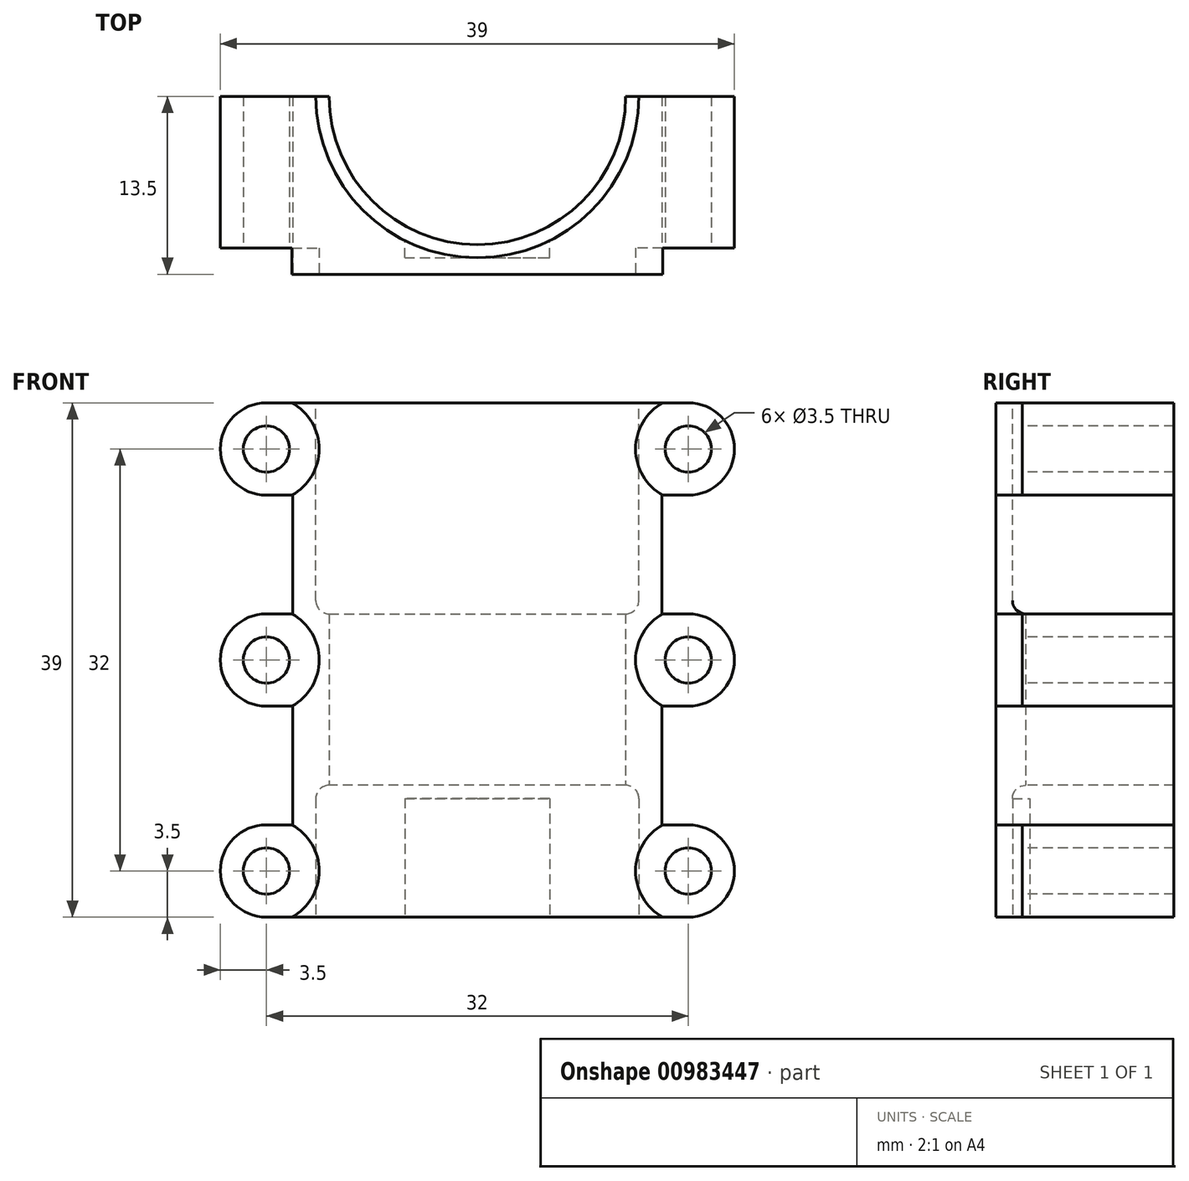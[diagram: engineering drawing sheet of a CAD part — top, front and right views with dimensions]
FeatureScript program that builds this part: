
annotation { "Feature Type Name" : "Feature", "Feature Type Description" : "" }
export const myFeature = defineFeature(function(context is Context, id is Id, definition is map)
    precondition{}
    {
        {
            var Q0;
            Q0=qCreatedBy(makeId("Top.planeOp"),FACE);
            var sketch = newSketch(context, id + "F0", { "sketchPlane" : qUnion([Q0])});
            skCircle(sketch, "E0", {"center": v(0, 0) * mm, "radius": 11.25 * mm});
            skSolve(sketch);
        }
        {
            var Q0;
            Q0=qSketchRegion(id+"F0",true);
            extrude(context, id + "F1", {"entities" : qUnion([Q0]), "depth" : 39 * mm, "offsetDistance" : 25 * mm});
        }
        {
            var Q0;
            Q0=makeQuery(id+"F1.opExtrude","CAP_FACE",FACE,{"disambiguationData":[OSD([sQuery(id+"F0.wireOp",EDGE,"E0")])],"isStart":false});
            var sketch = newSketch(context, id + "F2", { "sketchPlane" : qUnion([Q0])});
            skCircle(sketch, "E1", {"center": v(0, 0) * mm, "radius": 12.25 * mm});
            skSolve(sketch);
        }
        {
            var Q0;
            Q0=makeQuery(id+"F2.imprint","IMPRINT",FACE,{"disambiguationData":[TD([[makeQuery(id+"F2.imprint","IMPRINT",EDGE,{"derivedFrom":sQuery(id+"F2.wireOp",EDGE,"E1")}),1.0]])]});
            extrude(context, id + "F3", {"entities" : qUnion([Q0]), "operationType" : NewBodyOperationType.ADD, "oppositeDirection" : true, "depth" : 16 * mm, "offsetDistance" : 25 * mm});
        }
        {
            var Q0;
            Q0=makeQuery(id+"F1.opExtrude","CAP_FACE",FACE,{"disambiguationData":[OSD([sQuery(id+"F0.wireOp",EDGE,"E0")])],"isStart":true});
            var sketch = newSketch(context, id + "F4", { "sketchPlane" : qUnion([Q0])});
            skCircle(sketch, "E2", {"center": v(0, 0) * mm, "radius": 12.25 * mm});
            skSolve(sketch);
        }
        {
            var Q0;
            Q0=makeQuery(id+"F3.opExtrude","CAP_EDGE",EDGE,{"disambiguationData":[OSD([sQuery(id+"F2.wireOp",EDGE,"E1")])],"isStart":false});
            fillet(context, id + "F5", {"entities" : qUnion([Q0]), "radius" : 1 * mm, "tangentPropagation" : true, "allowEdgeOverflow" : false});
        }
        {
            var Q0;
            Q0=makeQuery(id+"F4.imprint","IMPRINT",FACE,{"disambiguationData":[TD([[makeQuery(id+"F4.imprint","IMPRINT",EDGE,{"derivedFrom":sQuery(id+"F4.wireOp",EDGE,"E2")}),1.0]])]});
            extrude(context, id + "F6", {"entities" : qUnion([Q0]), "operationType" : NewBodyOperationType.ADD, "oppositeDirection" : true, "depth" : 10 * mm, "offsetDistance" : 25 * mm});
        }
        {
            var Q0;
            Q0=makeQuery(id+"F6.opExtrude","CAP_EDGE",EDGE,{"disambiguationData":[OSD([sQuery(id+"F4.wireOp",EDGE,"E2")])],"isStart":false});
            fillet(context, id + "F7", {"entities" : qUnion([Q0]), "radius" : 1 * mm, "tangentPropagation" : true, "allowEdgeOverflow" : false});
        }
        {
            var Q0;
            {var subQ0=sQuery(id+"F0.wireOp",EDGE,"E0");Q0=makeQuery(id+"F6.boolean.opBoolean","MERGE",FACE,{"derivedFrom":[makeQuery(id+"F1.opExtrude","CAP_FACE",FACE,{"disambiguationData":[OSD([subQ0])],"isStart":true}),makeQuery(id+"F6.opExtrude","CAP_FACE",FACE,{"disambiguationData":[OSD([subQ0,sQuery(id+"F4.wireOp",EDGE,"E2")])],"isStart":true})]});}
            var sketch = newSketch(context, id + "F8", { "sketchPlane" : qUnion([Q0])});
            skLineSegment(sketch, "E3.bottom", {"start": v(-5.5, 12.25) * mm, "end": v(5.5, 12.25) * mm});
            skLineSegment(sketch, "E3.top", {"start": v(-5.5, 10.25) * mm, "end": v(5.5, 10.25) * mm});
            skLineSegment(sketch, "E3.left", {"start": v(-5.5, 12.25) * mm, "end": v(-5.5, 10.25) * mm});
            skLineSegment(sketch, "E3.right", {"start": v(5.5, 12.25) * mm, "end": v(5.5, 10.25) * mm});
            skPoint(sketch, "E3.middle", {"position": v(0, 11.25) * mm});
            skSolve(sketch);
        }
        {
            var Q0;
            {var subQ0=sQuery(id+"F8.wireOp",EDGE,"E3.left");var subQ1=sQuery(id+"F8.wireOp",EDGE,"E3.bottom");var subQ2=makeQuery(id+"F8.imprint","INTERSECT",VERTEX,{"derivedFrom":[subQ1,subQ0]});Q0=makeQuery(id+"F8.imprint","IMPRINT",FACE,{"disambiguationData":[TD([[makeQuery(id+"F8.imprint","IMPRINT",EDGE,{"disambiguationData":[TD([[subQ2,-1.0]])],"derivedFrom":subQ1}),-1.0]])]});}
            var Q1;
            {var subQ0=sQuery(id+"F8.wireOp",EDGE,"E3.right");var subQ1=sQuery(id+"F8.wireOp",EDGE,"E3.bottom");var subQ2=makeQuery(id+"F8.imprint","INTERSECT",VERTEX,{"derivedFrom":[subQ1,subQ0]});Q1=makeQuery(id+"F8.imprint","IMPRINT",FACE,{"disambiguationData":[TD([[makeQuery(id+"F8.imprint","IMPRINT",EDGE,{"disambiguationData":[TD([[subQ2,1.0]])],"derivedFrom":subQ1}),-1.0]])]});}
            extrude(context, id + "F9", {"entities" : qUnion([Q0, Q1]), "operationType" : NewBodyOperationType.ADD, "oppositeDirection" : true, "depth" : 9 * mm, "offsetDistance" : 25 * mm});
        }
        {
            var Q0;
            {var subQ0=sQuery(id+"F8.wireOp",EDGE,"E3.bottom");var subQ1=sQuery(id+"F4.wireOp",EDGE,"E2");var subQ2=sQuery(id+"F0.wireOp",EDGE,"E0");Q0=makeQuery(id+"F9.boolean.opBoolean","MERGE",FACE,{"derivedFrom":[makeQuery(id+"F6.boolean.opBoolean","MERGE",FACE,{"derivedFrom":[makeQuery(id+"F1.opExtrude","CAP_FACE",FACE,{"disambiguationData":[OSD([subQ2])],"isStart":true}),makeQuery(id+"F6.opExtrude","CAP_FACE",FACE,{"disambiguationData":[OSD([subQ2,subQ1])],"isStart":true})]}),makeQuery(id+"F9.opExtrude","CAP_FACE",FACE,{"disambiguationData":[OSD([subQ1,subQ0,sQuery(id+"F8.wireOp",EDGE,"E3.left")])],"isStart":true}),makeQuery(id+"F9.opExtrude","CAP_FACE",FACE,{"disambiguationData":[OSD([subQ1,subQ0,sQuery(id+"F8.wireOp",EDGE,"E3.right")])],"isStart":true})]});}
            var sketch = newSketch(context, id + "F10", { "sketchPlane" : qUnion([Q0])});
            skLineSegment(sketch, "E4.bottom", {"start": v(-7.5, -8.25) * mm, "end": v(7.5, -8.25) * mm});
            skLineSegment(sketch, "E4.top", {"start": v(-7.5, -12.25) * mm, "end": v(7.5, -12.25) * mm});
            skLineSegment(sketch, "E4.left", {"start": v(-7.5, -8.25) * mm, "end": v(-7.5, -12.25) * mm});
            skLineSegment(sketch, "E4.right", {"start": v(7.5, -8.25) * mm, "end": v(7.5, -12.25) * mm});
            skPoint(sketch, "E4.middle", {"position": v(0, -10.25) * mm});
            skSolve(sketch);
        }
        {
            var Q0;
            {var subQ0=sQuery(id+"F10.wireOp",EDGE,"E4.right");var subQ1=sQuery(id+"F10.wireOp",EDGE,"E4.top");var subQ2=makeQuery(id+"F10.imprint","INTERSECT",VERTEX,{"derivedFrom":[subQ1,subQ0]});Q0=makeQuery(id+"F10.imprint","IMPRINT",FACE,{"disambiguationData":[TD([[makeQuery(id+"F10.imprint","IMPRINT",EDGE,{"disambiguationData":[TD([[subQ2,1.0]])],"derivedFrom":subQ1}),1.0]])]});}
            var Q1;
            {var subQ0=sQuery(id+"F10.wireOp",EDGE,"E4.left");var subQ1=sQuery(id+"F10.wireOp",EDGE,"E4.top");var subQ2=makeQuery(id+"F10.imprint","INTERSECT",VERTEX,{"derivedFrom":[subQ1,subQ0]});Q1=makeQuery(id+"F10.imprint","IMPRINT",FACE,{"disambiguationData":[TD([[makeQuery(id+"F10.imprint","IMPRINT",EDGE,{"disambiguationData":[TD([[subQ2,-1.0]])],"derivedFrom":subQ1}),1.0]])]});}
            var Q2;
            {var subQ4=sQuery(id+"F10.wireOp",EDGE,"E4.bottom");Q2=makeQuery(id+"F10.imprint","IMPRINT",FACE,{"disambiguationData":[TD([[makeQuery(id+"F10.imprint","IMPRINT",EDGE,{"derivedFrom":subQ4}),-1.0]])]});}
            extrude(context, id + "F11", {"entities" : qUnion([Q0, Q1, Q2]), "operationType" : NewBodyOperationType.ADD, "oppositeDirection" : true, "depth" : 39 * mm, "offsetDistance" : 25 * mm});
        }
        {
            var Q0;
            Q0=makeQuery(id+"F11.opExtrude","SWEPT_FACE",FACE,{"disambiguationData":[OSD([sQuery(id+"F10.wireOp",EDGE,"E4.top")])]});
            var sketch = newSketch(context, id + "F12", { "sketchPlane" : qUnion([Q0])});
            skLineSegment(sketch, "E5.bottom", {"start": v(-11, 12) * mm, "end": v(-7.5, 12) * mm});
            skLineSegment(sketch, "E5.top", {"start": v(-11, 6.5) * mm, "end": v(-7.5, 6.5) * mm});
            skLineSegment(sketch, "E5.left", {"start": v(-11, 12) * mm, "end": v(-11, 6.5) * mm});
            skLineSegment(sketch, "E5.right", {"start": v(-7.5, 12) * mm, "end": v(-7.5, 6.5) * mm});
            skSolve(sketch);
        }
        {
            var Q0;
            Q0=makeQuery(id+"F12.imprint","IMPRINT",FACE,{"disambiguationData":[TD([[makeQuery(id+"F12.imprint","IMPRINT",EDGE,{"derivedFrom":sQuery(id+"F12.wireOp",EDGE,"E5.bottom")}),-1.0]])]});
            extrude(context, id + "F13", {"entities" : qUnion([Q0]), "operationType" : NewBodyOperationType.ADD, "depth" : 2 * mm, "offsetDistance" : 25 * mm, "hasSecondDirection" : true, "secondDirectionOppositeDirection" : true, "secondDirectionDepth" : 12 * mm});
        }
        {
            var Q0;
            Q0=makeQuery(id+"F11.opExtrude","SWEPT_FACE",FACE,{"disambiguationData":[OSD([sQuery(id+"F10.wireOp",EDGE,"E4.top")])]});
            var sketch = newSketch(context, id + "F14", { "sketchPlane" : qUnion([Q0])});
            skCircle(sketch, "E6", {"center": v(-0.06, 19) * mm, "radius": 6.5 * mm});
            skSolve(sketch);
        }
        {
            var Q0;
            Q0=makeQuery(id+"F14.imprint","IMPRINT",FACE,{"disambiguationData":[TD([[makeQuery(id+"F14.imprint","IMPRINT",EDGE,{"derivedFrom":sQuery(id+"F14.wireOp",EDGE,"E6")}),1.0]])]});
            extrude(context, id + "F15", {"entities" : qUnion([Q0]), "operationType" : NewBodyOperationType.ADD, "depth" : 2 * mm, "offsetDistance" : 25 * mm});
        }
        {
            var Q0;
            Q0=makeQuery(id+"F11.opExtrude","SWEPT_FACE",FACE,{"disambiguationData":[OSD([sQuery(id+"F10.wireOp",EDGE,"E4.top")])]});
            var sketch = newSketch(context, id + "F16", { "sketchPlane" : qUnion([Q0])});
            skLineSegment(sketch, "E7.bottom", {"start": v(-8, 27.5) * mm, "end": v(-4.5, 27.5) * mm});
            skLineSegment(sketch, "E7.top", {"start": v(-8, 31.5) * mm, "end": v(-4.5, 31.5) * mm});
            skLineSegment(sketch, "E7.left", {"start": v(-8, 27.5) * mm, "end": v(-8, 31.5) * mm});
            skLineSegment(sketch, "E7.right", {"start": v(-4.5, 27.5) * mm, "end": v(-4.5, 31.5) * mm});
            skSolve(sketch);
        }
        {
            var Q0;
            Q0=makeQuery(id+"F16.imprint","IMPRINT",FACE,{"disambiguationData":[TD([[makeQuery(id+"F16.imprint","IMPRINT",EDGE,{"derivedFrom":sQuery(id+"F16.wireOp",EDGE,"E7.bottom")}),1.0]])]});
            var Q1;
            {var subQ2=sQuery(id+"F16.wireOp",EDGE,"E7.right");Q1=makeQuery(id+"F16.imprint","IMPRINT",FACE,{"disambiguationData":[TD([[makeQuery(id+"F16.imprint","IMPRINT",EDGE,{"derivedFrom":subQ2}),1.0]])]});}
            extrude(context, id + "F17", {"entities" : qUnion([Q0, Q1]), "operationType" : NewBodyOperationType.ADD, "depth" : 6 * mm, "offsetDistance" : 25 * mm, "hasSecondDirection" : true, "secondDirectionOppositeDirection" : true, "secondDirectionDepth" : 16.7 * mm});
        }
        {
            var Q0;
            Q0=qCreatedBy(makeId("Front.planeOp"),FACE);
            var sketch = newSketch(context, id + "F18", { "sketchPlane" : qUnion([Q0])});
            skLineSegment(sketch, "E8.bottom", {"start": v(14, 0) * mm, "end": v(-14, 0) * mm});
            skLineSegment(sketch, "E8.top", {"start": v(14, 39) * mm, "end": v(-14, 39) * mm});
            skLineSegment(sketch, "E8.left", {"start": v(14, 0) * mm, "end": v(14, 39) * mm});
            skLineSegment(sketch, "E8.right", {"start": v(-14, 0) * mm, "end": v(-14, 39) * mm});
            skPoint(sketch, "E8.middle", {"position": v(0, 19.5) * mm});
            skSolve(sketch);
        }
        {
            var Q0;
            Q0=makeQuery(id+"F18.imprint","IMPRINT",FACE,{"disambiguationData":[TD([[makeQuery(id+"F18.imprint","IMPRINT",EDGE,{"derivedFrom":sQuery(id+"F18.wireOp",EDGE,"E8.bottom")}),-1.0]])]});
            extrude(context, id + "F19", {"entities" : qUnion([Q0]), "depth" : 13.5 * mm, "offsetDistance" : 25 * mm, "hasSecondDirection" : true, "secondDirectionOppositeDirection" : true, "secondDirectionDepth" : 12.2 * mm});
        }
        {
            var Q0;
            Q0=makeQuery(id+"F1.opExtrude","SWEPT_BODY",BODY,{"disambiguationData":[OSD([sQuery(id+"F0.wireOp",EDGE,"E0")])]});
            var Q1;
            Q1=makeQuery(id+"F19.opExtrude","SWEPT_BODY",BODY,{"disambiguationData":[OSD([sQuery(id+"F18.wireOp",EDGE,"E8.bottom"),sQuery(id+"F18.wireOp",EDGE,"E8.top"),sQuery(id+"F18.wireOp",EDGE,"E8.left"),sQuery(id+"F18.wireOp",EDGE,"E8.right")])]});
            booleanBodies(context, id + "F20", {"operationType" : BooleanOperationType.SUBTRACTION, "tools" : qUnion([Q0]), "targets" : qUnion([Q1])});
        }
        {
            var Q0;
            Q0=makeQuery(id+"F19.opExtrude","CAP_FACE",FACE,{"disambiguationData":[OSD([sQuery(id+"F18.wireOp",EDGE,"E8.bottom"),sQuery(id+"F18.wireOp",EDGE,"E8.top"),sQuery(id+"F18.wireOp",EDGE,"E8.left"),sQuery(id+"F18.wireOp",EDGE,"E8.right")])],"isStart":false});
            var sketch = newSketch(context, id + "F21", { "sketchPlane" : qUnion([Q0])});
            skLineSegment(sketch, "E9.bottom", {"start": v(16, 7) * mm, "end": v(-16, 7) * mm});
            skLineSegment(sketch, "E9.top", {"start": v(16, 0) * mm, "end": v(-16, 0) * mm});
            skLineSegment(sketch, "E9.left", {"start": v(19.5, 3.5) * mm, "end": v(19.5, 3.5) * mm});
            skLineSegment(sketch, "E9.right", {"start": v(-19.5, 3.5) * mm, "end": v(-19.5, 3.5) * mm});
            skPoint(sketch, "E9.middle", {"position": v(0, 3.5) * mm});
            skLineSegment(sketch, "E10.bottom", {"start": v(16, 39) * mm, "end": v(-16, 39) * mm});
            skLineSegment(sketch, "E10.top", {"start": v(16, 32) * mm, "end": v(-16, 32) * mm});
            skLineSegment(sketch, "E10.left", {"start": v(19.5, 35.5) * mm, "end": v(19.5, 35.5) * mm});
            skLineSegment(sketch, "E10.right", {"start": v(-19.5, 35.5) * mm, "end": v(-19.5, 35.5) * mm});
            skPoint(sketch, "E10.middle", {"position": v(0, 35.5) * mm});
            skPoint(sketch, "E11.visualSharp", {"position": v(-19.5, 0) * mm});
            skArc(sketch, "E11.filletArc", {"start": v(-19.5, 3.5) * mm, "mid": v(-18.47, 1.03) * mm, "end": v(-16, 0) * mm});
            skPoint(sketch, "E12.visualSharp", {"position": v(-19.5, 7) * mm});
            skArc(sketch, "E12.filletArc", {"start": v(-16, 7) * mm, "mid": v(-18.47, 5.97) * mm, "end": v(-19.5, 3.5) * mm});
            skPoint(sketch, "E13.visualSharp", {"position": v(-19.5, 32) * mm});
            skArc(sketch, "E13.filletArc", {"start": v(-19.5, 35.5) * mm, "mid": v(-18.47, 33.03) * mm, "end": v(-16, 32) * mm});
            skPoint(sketch, "E14.visualSharp", {"position": v(19.5, 39) * mm});
            skArc(sketch, "E14.filletArc", {"start": v(19.5, 35.5) * mm, "mid": v(18.47, 37.97) * mm, "end": v(16, 39) * mm});
            skPoint(sketch, "E15.visualSharp", {"position": v(19.5, 32) * mm});
            skArc(sketch, "E15.filletArc", {"start": v(16, 32) * mm, "mid": v(18.47, 33.03) * mm, "end": v(19.5, 35.5) * mm});
            skPoint(sketch, "E16.visualSharp", {"position": v(19.5, 0) * mm});
            skArc(sketch, "E16.filletArc", {"start": v(16, 0) * mm, "mid": v(18.47, 1.03) * mm, "end": v(19.5, 3.5) * mm});
            skPoint(sketch, "E17.visualSharp", {"position": v(-19.5, 39) * mm});
            skArc(sketch, "E17.filletArc", {"start": v(-16, 39) * mm, "mid": v(-18.47, 37.97) * mm, "end": v(-19.5, 35.5) * mm});
            skPoint(sketch, "E18.visualSharp", {"position": v(19.5, 7) * mm});
            skArc(sketch, "E18.filletArc", {"start": v(19.5, 3.5) * mm, "mid": v(18.47, 5.97) * mm, "end": v(16, 7) * mm});
            skCircle(sketch, "E19", {"center": v(-16, 35.5) * mm, "radius": 1.75 * mm});
            skCircle(sketch, "E20", {"center": v(16, 35.5) * mm, "radius": 1.75 * mm});
            skCircle(sketch, "E21", {"center": v(16, 3.5) * mm, "radius": 1.75 * mm});
            skCircle(sketch, "E22", {"center": v(-16, 3.5) * mm, "radius": 1.75 * mm});
            skLineSegment(sketch, "E23.bottom", {"start": v(16, 16) * mm, "end": v(-16, 16) * mm});
            skLineSegment(sketch, "E23.top", {"start": v(16, 23) * mm, "end": v(-16, 23) * mm});
            skLineSegment(sketch, "E23.left", {"start": v(19.5, 19.5) * mm, "end": v(19.5, 19.5) * mm});
            skLineSegment(sketch, "E23.right", {"start": v(-19.5, 19.5) * mm, "end": v(-19.5, 19.5) * mm});
            skPoint(sketch, "E23.middle", {"position": v(0, 19.5) * mm});
            skPoint(sketch, "E24.visualSharp", {"position": v(-19.5, 23) * mm});
            skArc(sketch, "E24.filletArc", {"start": v(-16, 23) * mm, "mid": v(-18.47, 21.97) * mm, "end": v(-19.5, 19.5) * mm});
            skPoint(sketch, "E25.visualSharp", {"position": v(-19.5, 16) * mm});
            skArc(sketch, "E25.filletArc", {"start": v(-19.5, 19.5) * mm, "mid": v(-18.47, 17.03) * mm, "end": v(-16, 16) * mm});
            skPoint(sketch, "E26.visualSharp", {"position": v(19.5, 16) * mm});
            skArc(sketch, "E26.filletArc", {"start": v(16, 16) * mm, "mid": v(18.47, 17.03) * mm, "end": v(19.5, 19.5) * mm});
            skPoint(sketch, "E27.visualSharp", {"position": v(19.5, 23) * mm});
            skArc(sketch, "E27.filletArc", {"start": v(19.5, 19.5) * mm, "mid": v(18.47, 21.97) * mm, "end": v(16, 23) * mm});
            skCircle(sketch, "E28", {"center": v(-16, 19.5) * mm, "radius": 1.75 * mm});
            skCircle(sketch, "E29", {"center": v(16, 19.5) * mm, "radius": 1.75 * mm});
            skSolve(sketch);
        }
        {
            var Q0;
            {var subQ0=sQuery(id+"F21.wireOp",EDGE,"E11.filletArc");Q0=makeQuery(id+"F21.imprint","IMPRINT",FACE,{"disambiguationData":[TD([[makeQuery(id+"F21.imprint","IMPRINT",EDGE,{"derivedFrom":subQ0}),1.0]])]});}
            var Q1;
            {var subQ5=sQuery(id+"F21.wireOp",EDGE,"E13.filletArc");Q1=makeQuery(id+"F21.imprint","IMPRINT",FACE,{"disambiguationData":[TD([[makeQuery(id+"F21.imprint","IMPRINT",EDGE,{"derivedFrom":subQ5}),1.0]])]});}
            var Q2;
            {var subQ5=sQuery(id+"F21.wireOp",EDGE,"E14.filletArc");Q2=makeQuery(id+"F21.imprint","IMPRINT",FACE,{"disambiguationData":[TD([[makeQuery(id+"F21.imprint","IMPRINT",EDGE,{"derivedFrom":subQ5}),1.0]])]});}
            var Q3;
            {var subQ4=sQuery(id+"F21.wireOp",EDGE,"E16.filletArc");Q3=makeQuery(id+"F21.imprint","IMPRINT",FACE,{"disambiguationData":[TD([[makeQuery(id+"F21.imprint","IMPRINT",EDGE,{"derivedFrom":subQ4}),1.0]])]});}
            var Q4;
            {var subQ4=sQuery(id+"F21.wireOp",EDGE,"E24.filletArc");var subQ6=sQuery(id+"F21.wireOp",EDGE,"E25.filletArc");var subQ7=makeQuery(id+"F21.imprint","INTERSECT",VERTEX,{"derivedFrom":[subQ4,subQ6]});Q4=makeQuery(id+"F21.imprint","IMPRINT",FACE,{"disambiguationData":[TD([[makeQuery(id+"F21.imprint","IMPRINT",EDGE,{"disambiguationData":[TD([[subQ7,1.0]])],"derivedFrom":subQ4}),1.0]])]});}
            var Q5;
            {var subQ0=sQuery(id+"F21.wireOp",EDGE,"E26.filletArc");var subQ6=sQuery(id+"F21.wireOp",EDGE,"E27.filletArc");var subQ7=makeQuery(id+"F21.imprint","INTERSECT",VERTEX,{"derivedFrom":[subQ0,subQ6]});Q5=makeQuery(id+"F21.imprint","IMPRINT",FACE,{"disambiguationData":[TD([[makeQuery(id+"F21.imprint","IMPRINT",EDGE,{"disambiguationData":[TD([[subQ7,1.0]])],"derivedFrom":subQ0}),1.0]])]});}
            extrude(context, id + "F22", {"entities" : qUnion([Q0, Q1, Q2, Q3, Q4, Q5]), "operationType" : NewBodyOperationType.ADD, "oppositeDirection" : true, "depth" : 25.7 * mm, "offsetDistance" : 25 * mm});
        }
        {
            var Q0;
            {var subQ0=sQuery(id+"F21.wireOp",EDGE,"E22");var subQ1=makeQuery(id+"F19.opExtrude","CAP_EDGE",EDGE,{"disambiguationData":[OSD([sQuery(id+"F18.wireOp",EDGE,"E8.right")])],"isStart":false});var subQ2=makeQuery(id+"F21.imprint","INTERSECT",VERTEX,{"disambiguationData":[OD(0.0)],"derivedFrom":[subQ1,subQ0]});Q0=makeQuery(id+"F21.imprint","IMPRINT",FACE,{"disambiguationData":[TD([[makeQuery(id+"F21.imprint","IMPRINT",EDGE,{"disambiguationData":[TD([[subQ2,-1.0]])],"derivedFrom":subQ0}),1.0]])]});}
            var Q1;
            {var subQ0=sQuery(id+"F21.wireOp",EDGE,"E21");var subQ1=makeQuery(id+"F19.opExtrude","CAP_EDGE",EDGE,{"disambiguationData":[OSD([sQuery(id+"F18.wireOp",EDGE,"E8.left")])],"isStart":false});var subQ2=makeQuery(id+"F21.imprint","INTERSECT",VERTEX,{"disambiguationData":[OD(0.0)],"derivedFrom":[subQ1,subQ0]});Q1=makeQuery(id+"F21.imprint","IMPRINT",FACE,{"disambiguationData":[TD([[makeQuery(id+"F21.imprint","IMPRINT",EDGE,{"disambiguationData":[TD([[subQ2,1.0]])],"derivedFrom":subQ0}),1.0]])]});}
            var Q2;
            {var subQ0=sQuery(id+"F21.wireOp",EDGE,"E20");var subQ1=makeQuery(id+"F19.opExtrude","CAP_EDGE",EDGE,{"disambiguationData":[OSD([sQuery(id+"F18.wireOp",EDGE,"E8.left")])],"isStart":false});var subQ2=makeQuery(id+"F21.imprint","INTERSECT",VERTEX,{"disambiguationData":[OD(0.0)],"derivedFrom":[subQ1,subQ0]});Q2=makeQuery(id+"F21.imprint","IMPRINT",FACE,{"disambiguationData":[TD([[makeQuery(id+"F21.imprint","IMPRINT",EDGE,{"disambiguationData":[TD([[subQ2,-1.0]])],"derivedFrom":subQ0}),1.0]])]});}
            var Q3;
            {var subQ0=sQuery(id+"F21.wireOp",EDGE,"E19");var subQ1=makeQuery(id+"F19.opExtrude","CAP_EDGE",EDGE,{"disambiguationData":[OSD([sQuery(id+"F18.wireOp",EDGE,"E8.right")])],"isStart":false});var subQ2=makeQuery(id+"F21.imprint","INTERSECT",VERTEX,{"disambiguationData":[OD(0.0)],"derivedFrom":[subQ1,subQ0]});Q3=makeQuery(id+"F21.imprint","IMPRINT",FACE,{"disambiguationData":[TD([[makeQuery(id+"F21.imprint","IMPRINT",EDGE,{"disambiguationData":[TD([[subQ2,1.0]])],"derivedFrom":subQ0}),1.0]])]});}
            var Q4;
            {var subQ0=sQuery(id+"F21.wireOp",EDGE,"E19");var subQ1=makeQuery(id+"F19.opExtrude","CAP_EDGE",EDGE,{"disambiguationData":[OSD([sQuery(id+"F18.wireOp",EDGE,"E8.right")])],"isStart":false});var subQ2=makeQuery(id+"F21.imprint","INTERSECT",VERTEX,{"disambiguationData":[OD(0.0)],"derivedFrom":[subQ1,subQ0]});Q4=makeQuery(id+"F21.imprint","IMPRINT",FACE,{"disambiguationData":[TD([[makeQuery(id+"F21.imprint","IMPRINT",EDGE,{"disambiguationData":[TD([[subQ2,-1.0]])],"derivedFrom":subQ0}),1.0]])]});}
            var Q5;
            {var subQ0=sQuery(id+"F21.wireOp",EDGE,"E28");var subQ1=makeQuery(id+"F19.opExtrude","CAP_EDGE",EDGE,{"disambiguationData":[OSD([sQuery(id+"F18.wireOp",EDGE,"E8.right")])],"isStart":false});var subQ2=makeQuery(id+"F21.imprint","INTERSECT",VERTEX,{"disambiguationData":[OD(0.0)],"derivedFrom":[subQ1,subQ0]});Q5=makeQuery(id+"F21.imprint","IMPRINT",FACE,{"disambiguationData":[TD([[makeQuery(id+"F21.imprint","IMPRINT",EDGE,{"disambiguationData":[TD([[subQ2,1.0]])],"derivedFrom":subQ0}),1.0]])]});}
            var Q6;
            {var subQ0=sQuery(id+"F21.wireOp",EDGE,"E29");var subQ1=makeQuery(id+"F19.opExtrude","CAP_EDGE",EDGE,{"disambiguationData":[OSD([sQuery(id+"F18.wireOp",EDGE,"E8.left")])],"isStart":false});var subQ2=makeQuery(id+"F21.imprint","INTERSECT",VERTEX,{"disambiguationData":[OD(0.0)],"derivedFrom":[subQ1,subQ0]});Q6=makeQuery(id+"F21.imprint","IMPRINT",FACE,{"disambiguationData":[TD([[makeQuery(id+"F21.imprint","IMPRINT",EDGE,{"disambiguationData":[TD([[subQ2,1.0]])],"derivedFrom":subQ0}),1.0]])]});}
            var Q7;
            {var subQ0=sQuery(id+"F21.wireOp",EDGE,"E28");var subQ1=makeQuery(id+"F19.opExtrude","CAP_EDGE",EDGE,{"disambiguationData":[OSD([sQuery(id+"F18.wireOp",EDGE,"E8.right")])],"isStart":false});var subQ2=makeQuery(id+"F21.imprint","INTERSECT",VERTEX,{"disambiguationData":[OD(0.0)],"derivedFrom":[subQ1,subQ0]});Q7=makeQuery(id+"F21.imprint","IMPRINT",FACE,{"disambiguationData":[TD([[makeQuery(id+"F21.imprint","IMPRINT",EDGE,{"disambiguationData":[TD([[subQ2,-1.0]])],"derivedFrom":subQ0}),1.0]])]});}
            extrude(context, id + "F23", {"entities" : qUnion([Q0, Q1, Q2, Q3, Q4, Q5, Q6, Q7]), "operationType" : NewBodyOperationType.REMOVE, "oppositeDirection" : true, "depth" : 25.7 * mm, "offsetDistance" : 25 * mm});
        }
        {
            var Q0;
            {var subQ0=sQuery(id+"F18.wireOp",EDGE,"E8.left");var subQ1=sQuery(id+"F18.wireOp",EDGE,"E8.right");Q0=makeQuery(id+"F22.boolean.opBoolean","MERGE",FACE,{"derivedFrom":[makeQuery(id+"F19.opExtrude","CAP_FACE",FACE,{"disambiguationData":[OSD([sQuery(id+"F18.wireOp",EDGE,"E8.bottom"),sQuery(id+"F18.wireOp",EDGE,"E8.top"),subQ0,subQ1])],"isStart":false}),makeQuery(id+"F22.opExtrude","CAP_FACE",FACE,{"disambiguationData":[OSD([subQ1,sQuery(id+"F21.wireOp",EDGE,"E11.filletArc"),sQuery(id+"F21.wireOp",EDGE,"E12.filletArc"),sQuery(id+"F21.wireOp",EDGE,"E22")])],"isStart":true}),makeQuery(id+"F22.opExtrude","CAP_FACE",FACE,{"disambiguationData":[OSD([subQ1,sQuery(id+"F21.wireOp",EDGE,"E13.filletArc"),sQuery(id+"F21.wireOp",EDGE,"E17.filletArc"),sQuery(id+"F21.wireOp",EDGE,"E19")])],"isStart":true}),makeQuery(id+"F22.opExtrude","CAP_FACE",FACE,{"disambiguationData":[OSD([subQ0,sQuery(id+"F21.wireOp",EDGE,"E14.filletArc"),sQuery(id+"F21.wireOp",EDGE,"E15.filletArc"),sQuery(id+"F21.wireOp",EDGE,"E20")])],"isStart":true}),makeQuery(id+"F22.opExtrude","CAP_FACE",FACE,{"disambiguationData":[OSD([subQ0,sQuery(id+"F21.wireOp",EDGE,"E16.filletArc"),sQuery(id+"F21.wireOp",EDGE,"E18.filletArc"),sQuery(id+"F21.wireOp",EDGE,"E21")])],"isStart":true})]});}
            var sketch = newSketch(context, id + "F24", { "sketchPlane" : qUnion([Q0])});
            skCircle(sketch, "E30", {"center": v(-16, 35.5) * mm, "radius": 4 * mm});
            skCircle(sketch, "E31", {"center": v(16, 35.5) * mm, "radius": 4 * mm});
            skCircle(sketch, "E32", {"center": v(16, 3.5) * mm, "radius": 4 * mm});
            skCircle(sketch, "E33", {"center": v(-16, 3.5) * mm, "radius": 4 * mm});
            skCircle(sketch, "E34", {"center": v(-16, 19.5) * mm, "radius": 4 * mm});
            skCircle(sketch, "E35", {"center": v(16, 19.5) * mm, "radius": 4 * mm});
            skSolve(sketch);
        }
        {
            var Q0;
            {var subQ9=sQuery(id+"F21.wireOp",EDGE,"E19");Q0=makeQuery(id+"F24.imprint","IMPRINT",FACE,{"disambiguationData":[TD([[makeQuery(id+"F24.imprint","IMPRINT",EDGE,{"derivedFrom":makeQuery(id+"F23.boolean.opBoolean","MERGE",EDGE,{"derivedFrom":[makeQuery(id+"F22.opExtrude","CAP_EDGE",EDGE,{"disambiguationData":[OSD([subQ9])],"isStart":true})],"fromTools":[makeQuery(id+"F23.opExtrude","CAP_EDGE",EDGE,{"disambiguationData":[OSD([subQ9])],"isStart":true})]})}),-1.0]])]});}
            var Q1;
            {var subQ7=sQuery(id+"F21.wireOp",EDGE,"E20");Q1=makeQuery(id+"F24.imprint","IMPRINT",FACE,{"disambiguationData":[TD([[makeQuery(id+"F24.imprint","IMPRINT",EDGE,{"derivedFrom":makeQuery(id+"F23.boolean.opBoolean","MERGE",EDGE,{"derivedFrom":[makeQuery(id+"F22.opExtrude","CAP_EDGE",EDGE,{"disambiguationData":[OSD([subQ7])],"isStart":true})],"fromTools":[makeQuery(id+"F23.opExtrude","CAP_EDGE",EDGE,{"disambiguationData":[OSD([subQ7])],"isStart":true})]})}),-1.0]])]});}
            var Q2;
            {var subQ9=sQuery(id+"F21.wireOp",EDGE,"E21");Q2=makeQuery(id+"F24.imprint","IMPRINT",FACE,{"disambiguationData":[TD([[makeQuery(id+"F24.imprint","IMPRINT",EDGE,{"derivedFrom":makeQuery(id+"F23.boolean.opBoolean","MERGE",EDGE,{"derivedFrom":[makeQuery(id+"F22.opExtrude","CAP_EDGE",EDGE,{"disambiguationData":[OSD([subQ9])],"isStart":true})],"fromTools":[makeQuery(id+"F23.opExtrude","CAP_EDGE",EDGE,{"disambiguationData":[OSD([subQ9])],"isStart":true})]})}),-1.0]])]});}
            var Q3;
            {var subQ9=sQuery(id+"F21.wireOp",EDGE,"E22");Q3=makeQuery(id+"F24.imprint","IMPRINT",FACE,{"disambiguationData":[TD([[makeQuery(id+"F24.imprint","IMPRINT",EDGE,{"derivedFrom":makeQuery(id+"F23.boolean.opBoolean","MERGE",EDGE,{"derivedFrom":[makeQuery(id+"F22.opExtrude","CAP_EDGE",EDGE,{"disambiguationData":[OSD([subQ9])],"isStart":true})],"fromTools":[makeQuery(id+"F23.opExtrude","CAP_EDGE",EDGE,{"disambiguationData":[OSD([subQ9])],"isStart":true})]})}),-1.0]])]});}
            var Q4;
            {var subQ6=sQuery(id+"F21.wireOp",EDGE,"E28");Q4=makeQuery(id+"F24.imprint","IMPRINT",FACE,{"disambiguationData":[TD([[makeQuery(id+"F24.imprint","IMPRINT",EDGE,{"derivedFrom":makeQuery(id+"F23.boolean.opBoolean","MERGE",EDGE,{"derivedFrom":[makeQuery(id+"F22.opExtrude","CAP_EDGE",EDGE,{"disambiguationData":[OSD([subQ6])],"isStart":true})],"fromTools":[makeQuery(id+"F23.opExtrude","CAP_EDGE",EDGE,{"disambiguationData":[OSD([subQ6])],"isStart":true})]})}),-1.0]])]});}
            var Q5;
            {var subQ6=sQuery(id+"F21.wireOp",EDGE,"E29");Q5=makeQuery(id+"F24.imprint","IMPRINT",FACE,{"disambiguationData":[TD([[makeQuery(id+"F24.imprint","IMPRINT",EDGE,{"derivedFrom":makeQuery(id+"F23.boolean.opBoolean","MERGE",EDGE,{"derivedFrom":[makeQuery(id+"F22.opExtrude","CAP_EDGE",EDGE,{"disambiguationData":[OSD([subQ6])],"isStart":true})],"fromTools":[makeQuery(id+"F23.opExtrude","CAP_EDGE",EDGE,{"disambiguationData":[OSD([subQ6])],"isStart":true})]})}),-1.0]])]});}
            extrude(context, id + "F25", {"entities" : qUnion([Q0, Q1, Q2, Q3, Q4, Q5]), "operationType" : NewBodyOperationType.REMOVE, "oppositeDirection" : true, "depth" : 2 * mm, "offsetDistance" : 25 * mm});
        }
        {
            var Q0;
            Q0=qCreatedBy(makeId("Front.planeOp"),FACE);
            var sketch = newSketch(context, id + "F26", { "sketchPlane" : qUnion([Q0])});
            skLineSegment(sketch, "E36.bottom", {"start": v(-25.06, -44.38) * mm, "end": v(25.06, -44.38) * mm});
            skLineSegment(sketch, "E36.top", {"start": v(-25.06, 44.38) * mm, "end": v(25.06, 44.38) * mm});
            skLineSegment(sketch, "E36.left", {"start": v(-25.06, -44.38) * mm, "end": v(-25.06, 44.38) * mm});
            skLineSegment(sketch, "E36.right", {"start": v(25.06, -44.38) * mm, "end": v(25.06, 44.38) * mm});
            skPoint(sketch, "E36.middle", {"position": v(0, 0) * mm});
            skSolve(sketch);
        }
        {
            var Q0;
            Q0 = qSketchRegion(id + "F26", true);
            extrude(context, id + "F27", {"entities" : qUnion([Q0]), "operationType" : NewBodyOperationType.REMOVE, "oppositeDirection" : true, "depth" : 25 * mm, "offsetDistance" : 25 * mm});
        }
    });
